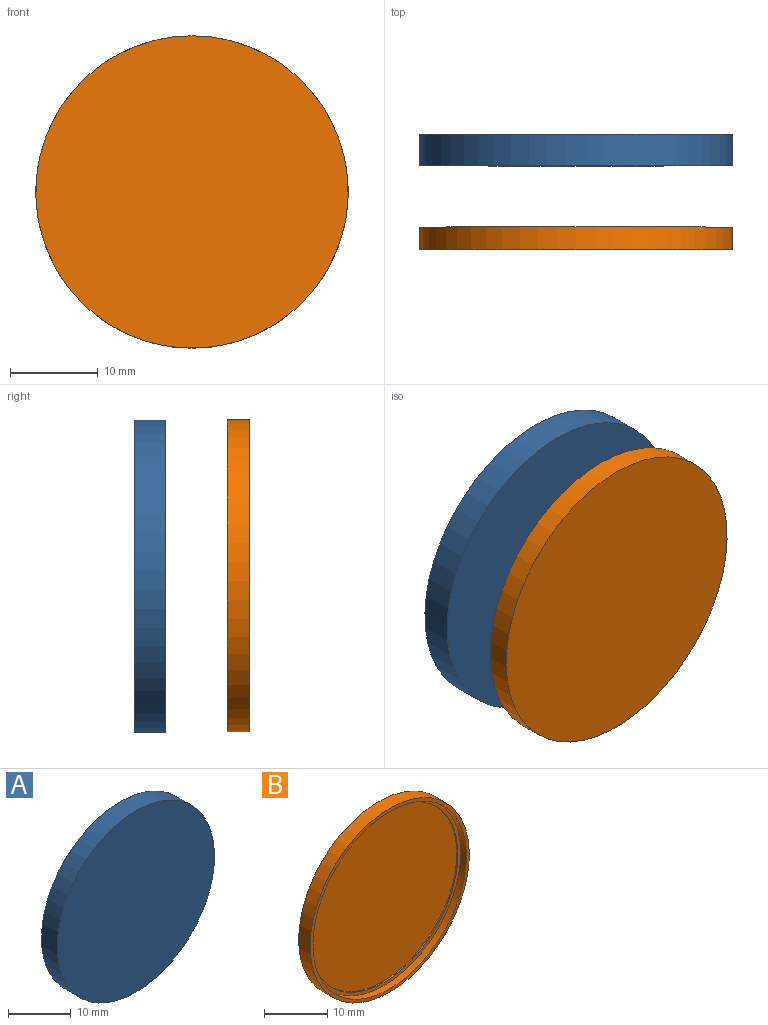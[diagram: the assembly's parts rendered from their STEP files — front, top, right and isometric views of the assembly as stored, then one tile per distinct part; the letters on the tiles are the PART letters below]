
ASSEMBLY  parts=2 mates=1
PART A: 6 faces, bbox 35.6x3.6x35.6 mm
  f0: cylinder r=17.78mm len=35.56mm, axis (0,1,0), area 397.3mm2, adj f1,f2
  f1: plane 35.56x35.56mm, normal (0,1,0), area 993.1mm2, adj f0
  f2: plane 35.56x35.56mm, normal (0,-1,0), area 993.1mm2, adj f0
  f3: plane 33.02x33.02mm, normal (0,-1,0), area 856.3mm2, adj f4
  f4: cylinder r=16.51mm len=33.02mm, axis (0,1,0), area 158.1mm2, adj f3,f5
  f5: plane 33.02x33.02mm, normal (0,1,0), area 856.3mm2, adj f4
PART B: 7 faces, bbox 35.6x2.6x35.6 mm
  f0: cylinder r=17.78mm len=35.56mm, axis (0,1,0), area 283.8mm2, adj f1,f2
  f1: plane 35.58x35.58mm, normal (0,-1,0), area 69.9mm2, adj f0,f4
  f2: plane 35.56x35.56mm, normal (0,1,0), area 993.1mm2, adj f0
  f3: plane 34.3x34.3mm, normal (0,-1,0), area 66.6mm2, adj f4,f6
  f4: cylinder r=17.14mm len=34.28mm, axis (0,-1,0), area 136.1mm2, adj f1,f3
  f5: plane 33.02x33.02mm, normal (0,-1,0), area 856.3mm2, adj f6
  f6: cylinder r=16.51mm len=33.02mm, axis (0,1,0), area 26.5mm2, adj f3,f5
PLACE A t=(0.95,-21.05,3.3)mm
PLACE B rot(axis=(1,0,0),180deg) t=(0.95,-34.14,3.3)mm
MATE slider A.f4 <-> B.f6  axis (0,-1,0) through (0.95,-22.07,3.3)mm
